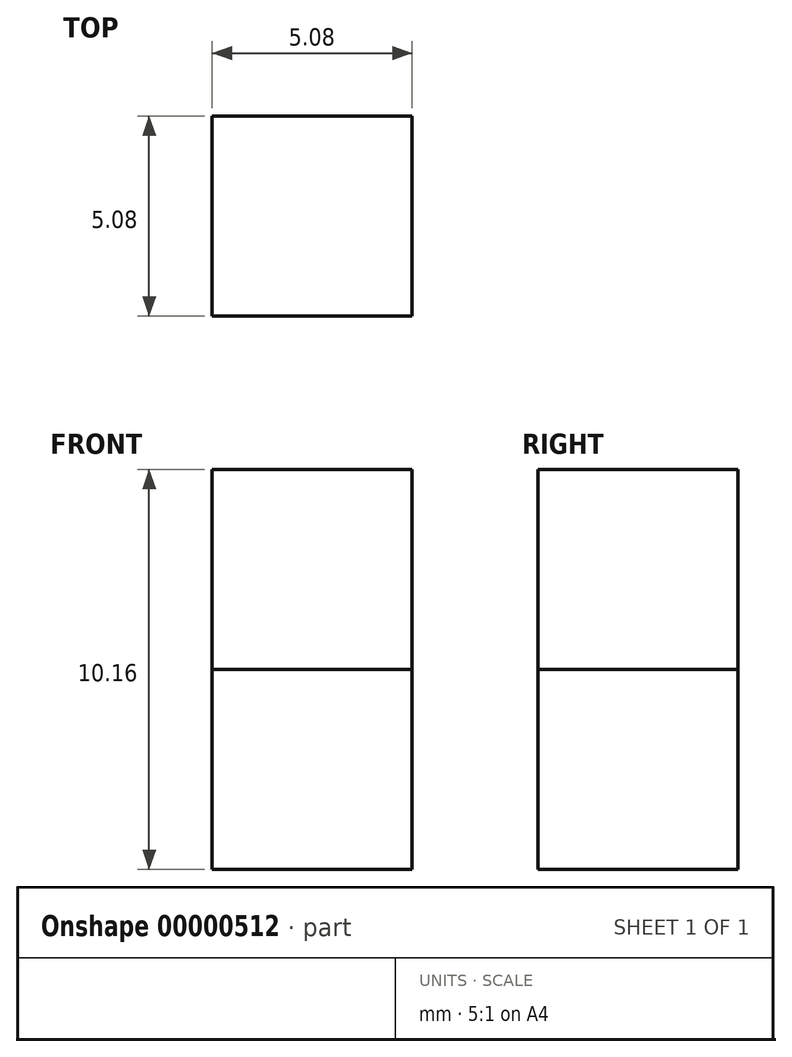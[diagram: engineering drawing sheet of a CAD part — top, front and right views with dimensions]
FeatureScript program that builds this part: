
annotation { "Feature Type Name" : "Feature", "Feature Type Description" : "" }
export const myFeature = defineFeature(function(context is Context, id is Id, definition is map)
    precondition{}
    {
        {
            var Q0;
            Q0=qCreatedBy(makeId("Front.planeOp"),FACE);
            var sketch = newSketch(context, id + "F0", { "sketchPlane" : qUnion([Q0])});
            skLineSegment(sketch, "E0.rect.bottom", {"start": v(2.79, -2.54) * mm, "end": v(-2.3, -2.54) * mm});
            skLineSegment(sketch, "E0.rect.top", {"start": v(2.79, 2.54) * mm, "end": v(-2.3, 2.54) * mm});
            skLineSegment(sketch, "E0.rect.left", {"start": v(2.79, -2.54) * mm, "end": v(2.79, 2.54) * mm});
            skLineSegment(sketch, "E0.rect.right", {"start": v(-2.3, -2.54) * mm, "end": v(-2.3, 2.54) * mm});
            skPoint(sketch, "E0.rect.middle", {"position": v(0.25, 0) * mm});
            skSolve(sketch);
        }
        {
            var Q0;
            Q0=makeQuery(id+"F0.imprint","IMPRINT",FACE,{"disambiguationData":[TD([[makeQuery(id+"F0.imprint","IMPRINT",EDGE,{"derivedFrom":sQuery(id+"F0.wireOp",EDGE,"E0.rect.bottom")}),-1.0]])]});
            extrude(context, id + "F1", {"entities" : qUnion([Q0]), "depth" : 2.54 * mm});
        }
        {
            var Q0;
            Q0=makeQuery(id+"F1.opExtrude","CAP_FACE",FACE,{"disambiguationData":[OSD([sQuery(id+"F0.wireOp",EDGE,"E0.rect.bottom"),sQuery(id+"F0.wireOp",EDGE,"E0.rect.top"),sQuery(id+"F0.wireOp",EDGE,"E0.rect.left"),sQuery(id+"F0.wireOp",EDGE,"E0.rect.right")])],"isStart":true});
            extrude(context, id + "F2", {"entities" : qUnion([Q0]), "operationType" : NewBodyOperationType.ADD, "depth" : 2.54 * mm});
        }
        {
            var Q0;
            Q0=makeQuery(id+"F1.opExtrude","SWEPT_BODY",BODY,{"disambiguationData":[OSD([sQuery(id+"F0.wireOp",EDGE,"E0.rect.bottom"),sQuery(id+"F0.wireOp",EDGE,"E0.rect.top"),sQuery(id+"F0.wireOp",EDGE,"E0.rect.left"),sQuery(id+"F0.wireOp",EDGE,"E0.rect.right")])]});
            var Q1;
            Q1=makeQuery(id+"F1.opExtrude","CAP_EDGE",EDGE,{"disambiguationData":[OSD([sQuery(id+"F0.wireOp",EDGE,"E0.rect.top")])],"isStart":false});
            transform(context, id + "F3", {"entities" : qUnion([Q0]), "transformType" : TransformType.ROTATION, "transformAxis" : qUnion([Q1]), "angle" : 90 * degree, "oppositeDirection" : true, "makeCopy" : true});
        }
    });
